# Revit family: EN 100 VJR
name_source: partatom
category: Equipement spécialisé
units: mm (PartAtom-declared; Revit-internal decimal feet)

## family parameters
Basée sur le plan de construction = Non
Cote de connecteur circulaire = Utiliser le diamètre
Couper avec des vides une fois chargée = Non
Numéro OmniClass = 23.50.00.00
Partagée = Non
Point de calcul de pièce = Non
Titre OmniClass = Conveying Systems & Material Handling
Toujours verticalement = Oui
Type d'élément = Normal

## types (1)
- 100 VJR
    Average consumption (L/h) = 0
    Average consumption (l/day) = 0.00 m
    CO2 emissions (g/kWh) = 0
    Counterweight offset (turret at 90°) = 0.09 m
    Créé par = ATLANCAD
    Elévation par défaut = 0.00 m
    Engine norm = A préciser
    External turning radius = 2.09 m
    Fabricant = MANITOU
    Floor height (access) = 0.51 m
    Ground clearance = 0.02 m
    Ground clearance at centre of wheelbase = 0.09 m
    I.C. Engine power rating - Power (ch) = 0
    I.C. Engine power rating - Power (kW) = 0
    Internal turning radius (over tyres) = 0.59 m
    Jib length = 1.50 m
    Max. lifting height = 9.85 m
    Max. outreach = 3.15 m
    Modèle = 100 VJR
    Noise to environment (LwA) = 0
    Number of people (inside) = 2
    Number of people (outside) = 1
    Overall height (stowed) = 1.99 m
    Overall height (transport) = 2.00 m
    Overall lenght (stowed) = 2.80 m
    Overall lenght (transport) = 2.81 m
    Overhang = 6.67 m
    Permissible leveling = 2.00°
    Platform capacity = 200.00 kg
    Platform dimensions (length) = 1.11 m
    Platform dimensions (width) = 0.93 m
    Platform weight = 2650.00 kg
    URL = www.manitou.fr
    Wheelbase = 1.20 m
    Width = 0.99 m
